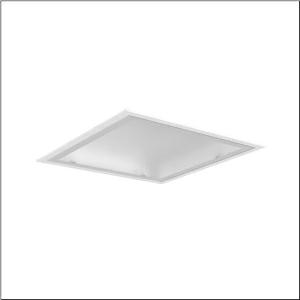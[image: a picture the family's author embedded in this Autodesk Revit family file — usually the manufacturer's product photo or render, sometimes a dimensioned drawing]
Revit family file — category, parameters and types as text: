
# Revit family: mira_11_51fr127a441a
name_source: partatom
category: Lighting Fixtures
units: mm (PartAtom-declared; Revit-internal decimal feet)

## family parameters
Cut with Voids When Loaded = No
Host = Face
Light Source = No
Part Type = Normal
Room Calculation Point = No
Round Connector Dimension = Use Diameter
Shared = No

## types (1)
- Mira 11 (1 x LED, 4610 lm, 37 W, 4000K)
    Apparent Load = 37 VA
    CIE Flux Codes = 51 82 97 100 100
    Color Rendering = 80
    Color Temperature = 4000K
    Default Elevation = 1800 mm
    Description = Mira 11, clean room luminaire, primary light control with reflector, primary optical cover: cover, of toughened safety glass, light emission: direct distribution, primary light characteristic: symmetric, installation type: recessed, LED, rated luminous flux: 4.610lm, luminous efficacy: 125lm/W, light colour: 840, colour temperature: 4000K, control gear: ON/OFF, with terminal, 3-pole, max. 2.5mm², mains connection: 230V, AC, 50/60Hz, rated input power: 37W, luminaire housing, of sheet steel, coated, pure white (RAL 9010), with concealed magnets, module: M625, length: 623mm, width: 623mm, height: 90mm, protection rating (complete): IP65, insulation class (complete): insulation class I (protective earthing), certification: CE, UKCA, permissible operating ambient temperature: -5..+40°C, standard: EN 50419, packaging unit: 1 piece
    Height = 0 mm  [stored 0 ft]
    Lamp = 1 x LED
    Lamp Light Flux = 4610 lm
    Lamp Power = 37 W
    Lamp count = 1
    Length = 625 mm
    Luminous efficacy = 125 lm/W
    Manufacturer = Siteco
    ModVariant = No
    Model = 51FR127A441A
    Mounting Place = Ceiling
    Mounting Type = Recessed
    Number of Poles = 1
    OnlyDefault = Yes
    Power Factor = 1
    Product Name = Mira 11
    Product group = clean room luminaire | ceiling recessed
    ProductGroupID = 402
    Protection Class = Protection class I
    Protection Degree = IP 65
    RLX_Detail_Level = 1
    RLX_Emergency_Light_Flux = 0 lm
    RLX_Emergency_Type = 0
    RLX_Emergency_Type_DB = No
    RlxData = <blob elided: 19273 chars, md5=356acbbf>
    Socket = socket
    Standby Power = 0 W
    System Light Flux = 4610 lm
    System Power = 37 W
    Type Comments = Product without accessories
    Type Image = l_1006636.jpg
    URL = http://relux.com
    VarID = ---
    Voltage = 0 V
    Weight = 0.00 kg
    Width = 625 mm

note: [stored X ft] marks values corroborated as IEEE doubles in the binary element streams (Revit-internal decimal feet)

## geometry (parser evidence)
native form markers: Blend x4, Sweep x9
no freeform markers — native parametric forms only
